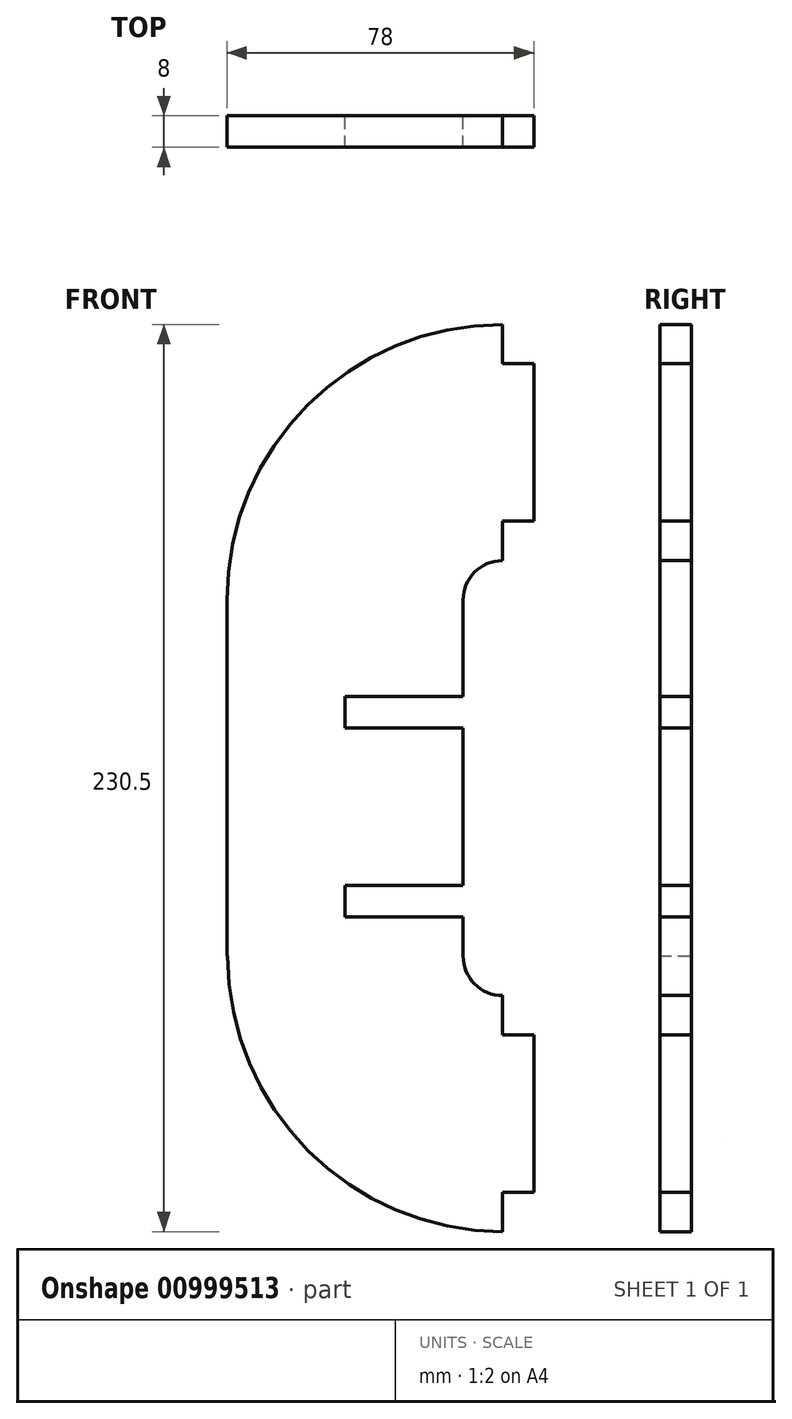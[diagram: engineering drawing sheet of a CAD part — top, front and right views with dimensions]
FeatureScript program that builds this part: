
annotation { "Feature Type Name" : "Feature", "Feature Type Description" : "" }
export const myFeature = defineFeature(function(context is Context, id is Id, definition is map)
    precondition{}
    {
        {
            var Q0;
            Q0=qCreatedBy(makeId("Front.planeOp"),FACE);
            var sketch = newSketch(context, id + "F0", { "sketchPlane" : qUnion([Q0])});
            skLineSegment(sketch, "E0.bottom", {"start": v(-30, -45.25) * mm, "end": v(30, -45.25) * mm});
            skLineSegment(sketch, "E0.top", {"start": v(-30, 45.25) * mm, "end": v(30, 45.25) * mm});
            skLineSegment(sketch, "E0.left", {"start": v(-30, -45.25) * mm, "end": v(-30, 45.25) * mm});
            skLineSegment(sketch, "E0.right", {"start": v(30, -45.25) * mm, "end": v(30, 45.25) * mm});
            skPoint(sketch, "E0.middle", {"position": v(0, 0) * mm});
            skArc(sketch, "E1", {"start": v(30, -45.25) * mm, "mid": v(32.93, -52.32) * mm, "end": v(40, -55.25) * mm});
            skArc(sketch, "E2", {"start": v(30, 45.25) * mm, "mid": v(32.93, 52.32) * mm, "end": v(40, 55.25) * mm});
            skLineSegment(sketch, "E3.bottom", {"start": v(30, -27.25) * mm, "end": v(0, -27.25) * mm});
            skLineSegment(sketch, "E3.top", {"start": v(30, -35.25) * mm, "end": v(0, -35.25) * mm});
            skLineSegment(sketch, "E3.left", {"start": v(30, -27.25) * mm, "end": v(30, -35.25) * mm});
            skLineSegment(sketch, "E3.right", {"start": v(0, -27.25) * mm, "end": v(0, -35.25) * mm});
            skLineSegment(sketch, "E4.bottom", {"start": v(30, 12.75) * mm, "end": v(0, 12.75) * mm});
            skLineSegment(sketch, "E4.top", {"start": v(30, 20.75) * mm, "end": v(0, 20.75) * mm});
            skLineSegment(sketch, "E4.left", {"start": v(30, 12.75) * mm, "end": v(30, 20.75) * mm});
            skLineSegment(sketch, "E4.right", {"start": v(0, 12.75) * mm, "end": v(0, 20.75) * mm});
            skArc(sketch, "E5", {"start": v(-30, 45.25) * mm, "mid": v(-9.5, 94.75) * mm, "end": v(40, 115.25) * mm});
            skArc(sketch, "E6", {"start": v(-29.78, -45.03) * mm, "mid": v(-9.43, -94.6) * mm, "end": v(40, -115.25) * mm});
            skLineSegment(sketch, "E7", {"start": v(40, -115.25) * mm, "end": v(40, -55.25) * mm});
            skLineSegment(sketch, "E8", {"start": v(40, 115.25) * mm, "end": v(40, 55.25) * mm});
            skLineSegment(sketch, "E9.bottom", {"start": v(40, 105.25) * mm, "end": v(48, 105.25) * mm});
            skLineSegment(sketch, "E9.top", {"start": v(40, 65.25) * mm, "end": v(48, 65.25) * mm});
            skLineSegment(sketch, "E9.left", {"start": v(40, 105.25) * mm, "end": v(40, 65.25) * mm});
            skLineSegment(sketch, "E9.right", {"start": v(48, 105.25) * mm, "end": v(48, 65.25) * mm});
            skLineSegment(sketch, "E10.bottom", {"start": v(40, -65.25) * mm, "end": v(48, -65.25) * mm});
            skLineSegment(sketch, "E10.top", {"start": v(40, -105.25) * mm, "end": v(48, -105.25) * mm});
            skLineSegment(sketch, "E10.left", {"start": v(40, -65.25) * mm, "end": v(40, -105.25) * mm});
            skLineSegment(sketch, "E10.right", {"start": v(48, -65.25) * mm, "end": v(48, -105.25) * mm});
            skSolve(sketch);
        }
        {
            var Q0;
            {var subQ1=sQuery(id+"F0.wireOp",EDGE,"E9.bottom");Q0=makeQuery(id+"F0.imprint","IMPRINT",FACE,{"disambiguationData":[TD([[makeQuery(id+"F0.imprint","IMPRINT",EDGE,{"derivedFrom":subQ1}),-1.0]])]});}
            var Q1;
            {var subQ1=sQuery(id+"F0.wireOp",EDGE,"E10.bottom");Q1=makeQuery(id+"F0.imprint","IMPRINT",FACE,{"disambiguationData":[TD([[makeQuery(id+"F0.imprint","IMPRINT",EDGE,{"derivedFrom":subQ1}),-1.0]])]});}
            var Q2;
            {var subQ6=sQuery(id+"F0.wireOp",EDGE,"E1");Q2=makeQuery(id+"F0.imprint","IMPRINT",FACE,{"disambiguationData":[TD([[makeQuery(id+"F0.imprint","IMPRINT",EDGE,{"derivedFrom":subQ6}),-1.0]])]});}
            var Q3;
            Q3=makeQuery(id+"F0.imprint","IMPRINT",FACE,{"disambiguationData":[TD([[makeQuery(id+"F0.imprint","IMPRINT",EDGE,{"derivedFrom":sQuery(id+"F0.wireOp",EDGE,"E0.top")}),1.0]])]});
            var Q4;
            {var subQ3=sQuery(id+"F0.wireOp",EDGE,"E0.top");Q4=makeQuery(id+"F0.imprint","IMPRINT",FACE,{"disambiguationData":[TD([[makeQuery(id+"F0.imprint","IMPRINT",EDGE,{"derivedFrom":subQ3}),-1.0]])]});}
            extrude(context, id + "F1", {"entities" : qUnion([Q0, Q1, Q2, Q3, Q4]), "depth" : 8 * mm, "offsetDistance" : 25 * mm});
        }
    });
